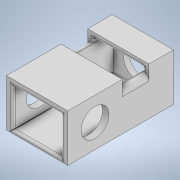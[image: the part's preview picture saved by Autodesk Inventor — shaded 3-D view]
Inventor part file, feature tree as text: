
AUTODESK INVENTOR PART (.ipt)
format: ipt  version: 2020.4 (Build 244396010, 396A)  size: 365,056 bytes
history: native  units: in
note: dims shown in document units (in); Inventor stores cm internally (conversion verified against a paired STEP export)
features: extrude x12, sketch x12, projected_geometry x12, fillet x4
ambient origin geometry x8: Origin, YZ Plane, XZ Plane, XY Plane, X Axis, Y Axis, Z Axis, Center Point
bodies: Solid1 (feature_tree)
feature tree (40):
  extrude  "Extrusion1"  Depth=3.7402in
  extrude  "Extrusion2"  Depth=0.0984in
  extrude  "Extrusion3"  Depth=1.378in
  extrude  "Extrusion4"  Depth=0.8661in
  extrude  "Extrusion5"  Depth=1.811in TaperAngle=0.0deg
  extrude  "Extrusion6"  Depth=0.2362in TaperAngle=0.0deg
  extrude  "Extrusion7"  Depth=0.0984in TaperAngle=0.0deg
  extrude  "Extrusion9"  Depth=0.0197in
  extrude  "Extrusion11"  Depth=0.8563in
  extrude  "Extrusion12"  Depth=0.6693in
  extrude  "Extrusion15"  TaperAngle=180.0deg  [1 undecoded]
  fillet  "Fillet1"  Radius=0.0197in
  fillet  "Fillet3"  Radius=0.0197in
  fillet  "Fillet4"  Radius=0.1181in
  fillet  "Fillet5"  Radius=0.0197in
  extrude  "Extrusion16"  Depth=0.3937in TaperAngle=0.0deg
  sketch  "Sketch1"  dims[d0=1.9685in d1=3.7402in]
  sketch  "Sketch2"  dims[d2=1.5748in d3=0.0in d4=0.0984in]
  projected_geometry  "Projected Loop1"
  sketch  "Sketch3"  dims[d5=1.7717in d6=1.378in]
  projected_geometry  "Projected Loop2"
  sketch  "Sketch4"  dims[d7=3.5433in d8=0.0in d9=0.8661in]
  projected_geometry  "Projected Loop3"
  sketch  "Sketch5"  dims[d10=1.811in d11=0.2362in d12=0.0in]
  projected_geometry  "Projected Loop4"
  sketch  "Sketch6"  dims[d13=0.9843in d14=0.2362in d15=0.0in]
  projected_geometry  "Projected Loop5"
  sketch  "Sketch7"  dims[d16=0.0984in d17=0.0in d18=0.0984in d19=0.0in]
  projected_geometry  "Projected Loop6"
  projected_geometry  "Projected Loop7"
  sketch  "Sketch10"  dims[d20=0.0984in d21=0.0in d29=0.0197in]
  projected_geometry  "Projected Loop9"
  sketch  "Sketch11"  dims[d30=0.0984in d31=0.0in d49=0.8563in]
  projected_geometry  "Projected Loop10"
  sketch  "Sketch12"  dims[d50=0.8563in d51=0.6693in]
  projected_geometry  "Projected Loop11"
  sketch  "Sketch16"  dims[d52=0.3937in d53=0.0in d54=180.0deg d55=0.0197in d56=0.0197in d58=0.1181in d59=0.0197in]
  projected_geometry  "Projected Loop15"
  sketch  "Sketch18"  dims[d60=0.3937in d61=0.0in d66=0.3937in d67=0.0in d68=0.1969in d70=0.1181in d71=0.1181in d73=0.0787in d74=0.9843in d75=0.0in d76=0.0in]
  projected_geometry  "Projected Loop17"
note: 1 required parameter value undecoded (feature->parameter linkage not recoverable at this tier; creation-order binding heuristic only, values carry confidence <= 0.55)
